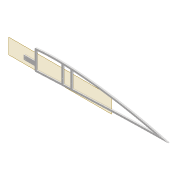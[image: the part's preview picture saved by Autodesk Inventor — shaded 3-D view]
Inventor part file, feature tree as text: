
AUTODESK INVENTOR PART (.ipt)
format: ipt  version: 2022 (Build 260153000, 153)  size: 418,304 bytes
history: native  units: mm
features: extrude x8, sketch x7, projected_geometry x6, fillet x2, shell x1, plane x1
ambient origin geometry x8: Origin, YZ Plane, XZ Plane, XY Plane, X Axis, Y Axis, Z Axis, Center Point
bodies: Solid1 (feature_tree)
feature tree (25):
  extrude  "Extrusion1"  Depth=5.0mm
  shell  "Shell1"  Thickness=2.0mm
  extrude  "Extrusion8"  Depth=5.9mm
  extrude  "Extrusion3"  Depth=10.0mm TaperAngle=0.0deg
  extrude  "Extrusion4"  Depth=2.0mm
  fillet  "Fillet1"  Radius=80.0mm
  sketch  "Sketch10"  dims[d22=4.0mm d23=0.0mm d31=2.0mm d62=80.0mm]
  extrude  "Extrusion5"  Depth=4.0mm TaperAngle=0.0deg
  plane  "Work Plane2"
  extrude  "Extrusion10"  Depth=12.0mm
  fillet  "Fillet2"  Radius=5.0mm
  extrude  "Extrusion11"  Depth=0.5mm
  extrude  "Extrusion12"  Depth=0.5mm
  sketch  "Sketch3"  dims[d0=4.0mm d1=0.0mm d2=5.0mm d7=2.0mm]
  sketch  "Sketch8"  dims[d8=2.0mm d9=5.9mm]
  sketch  "Sketch9"  dims[d13=10.0mm d14=0.0mm d16=10.0mm d17=0.0mm]
  projected_geometry  "Projected Loop4"
  projected_geometry  "Projected Loop10"
  sketch  "Sketch24"  dims[d63=6.0mm d64=4.0mm d65=0.0mm]
  projected_geometry  "Projected Loop11"
  projected_geometry  "Projected Loop12"
  projected_geometry  "Projected Loop13"
  sketch  "Sketch28"  dims[d66=3.0mm d67=12.0mm d68=5.0mm]
  projected_geometry  "Projected Loop14"
  sketch  "Sketch29"  dims[d69=5.0mm d74=12.0mm d75=30.0mm d76=3.05mm d77=5.0mm d78=10.0mm d79=0.0mm d80=2.0mm d81=100.0mm d82=20.0mm d83=1.6mm d84=1.6mm d85=2.5mm d86=2.5mm d87=0.5mm d88=10.0mm d89=0.0mm d90=10.0mm d91=0.0mm]
